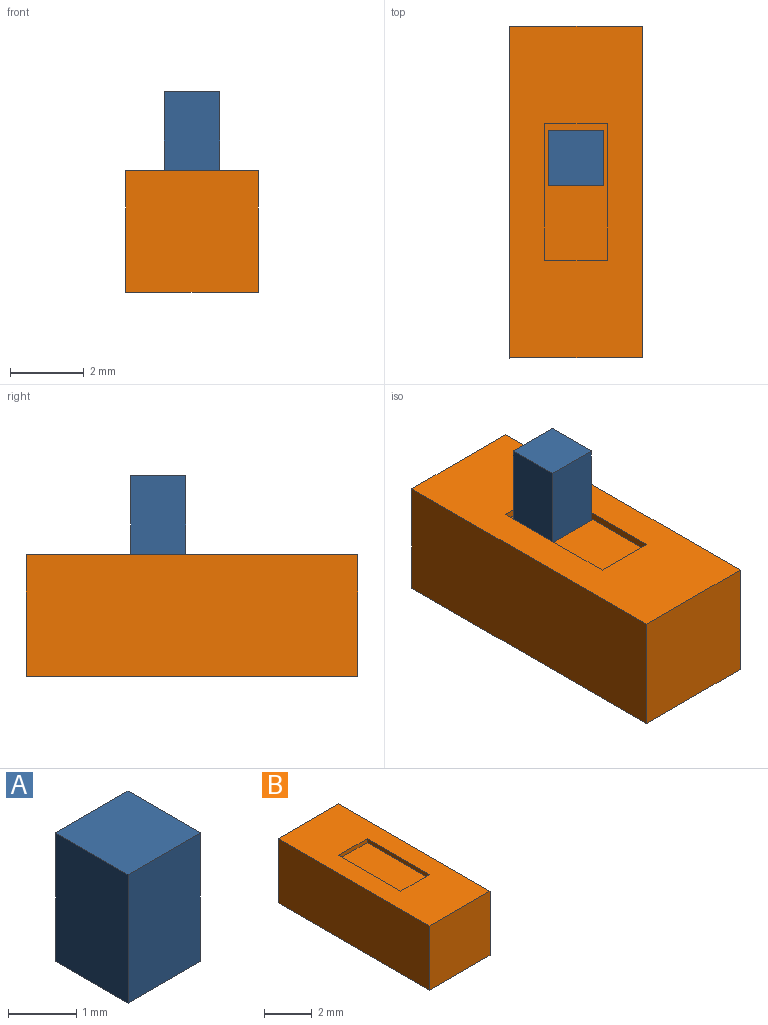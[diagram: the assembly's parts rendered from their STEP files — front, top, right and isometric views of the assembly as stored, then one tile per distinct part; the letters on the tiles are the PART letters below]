
ASSEMBLY  parts=2 mates=1
PART A: 6 faces, bbox 1.5x1.5x2.3 mm
  f0: plane 2.3x1.5mm, normal (0,-1,0), area 3.4mm2, adj f1,f3,f4,f5
  f1: plane 2.3x1.5mm, normal (1,0,0), area 3.4mm2, adj f0,f2,f4,f5
  f2: plane 2.3x1.5mm, normal (0,1,0), area 3.4mm2, adj f1,f3,f4,f5
  f3: plane 2.3x1.5mm, normal (-1,0,0), area 3.4mm2, adj f0,f2,f4,f5
  f4: plane 1.5x1.5mm, normal (0,0,1), area 2.3mm2, adj f0,f1,f2,f3
  f5: plane 1.5x1.5mm, normal (0,0,-1), area 2.3mm2, adj f0,f1,f2,f3
PART B: 11 faces, bbox 3.6x9x3.3 mm
  f0: plane 9x3.6mm, normal (0,0,1), area 26.1mm2, adj f1,f2,f3,f4,f6,f7,f8,f9
  f1: plane 9x3.3mm, normal (1,0,0), area 29.7mm2, adj f0,f2,f4,f5
  f2: plane 3.6x3.3mm, normal (0,1,0), area 11.9mm2, adj f0,f1,f3,f5
  f3: plane 9x3.3mm, normal (-1,0,0), area 29.7mm2, adj f0,f2,f4,f5
  f4: plane 3.6x3.3mm, normal (0,-1,0), area 11.9mm2, adj f0,f1,f3,f5
  f5: plane 9x3.6mm, normal (0,0,-1), area 32.4mm2, adj f1,f2,f3,f4
  f6: plane 3.7x0.2mm, normal (-1,0,0), area 0.7mm2, adj f0,f7,f9,f10
  f7: plane 1.7x0.2mm, normal (0,-1,0), area 0.3mm2, adj f0,f6,f8,f10
  f8: plane 3.7x0.2mm, normal (1,0,0), area 0.7mm2, adj f0,f7,f9,f10
  f9: plane 1.7x0.2mm, normal (0,1,0), area 0.3mm2, adj f0,f6,f8,f10
  f10: plane 3.7x1.7mm, normal (0,0,1), area 6.3mm2, adj f6,f7,f8,f9
PLACE A rot(axis=(0,-1,0),0deg) t=(0.48,4.94,-9.6)mm
PLACE B rot(axis=(0,-1,0),0deg) t=(0.48,3.02,-9.65)mm
MATE slider B.f7 <-> A.f2  axis (0,-1,0) through (0.48,4.87,-8.1)mm
